# Revit family: Gira_045401
name_source: partatom
category: Electrical Fixtures
revit_build: Autodesk Revit 2017 (Build: 20160225_1515(x64)
units: mm (PartAtom-declared; Revit-internal decimal feet)

## family parameters
Cut with Voids When Loaded = No
Host = Face
Maintain Annotation Orientation = Yes
Part Type = Normal
Room Calculation Point = No
Round Connector Dimension = Use Diameter
Shared = No

## types (1)
- SCHUKO HC System 55 cr.white
    Available = No
    BIM (1) = https://media.stage.bim.site
    Category = Socket outlet
    Cremeweiß glänzend = Cremeweiß glänzend
    Data sheet (1) = https://katalog.gira.de
    Default Elevation = 1219 mm
    Description = SCHUKO HC Sys55 CW,SCHUKO socket outlet 16 A 250 V~ with hinged cover,,cream white glossy,Notes :,- In conjunction with the seal set and frame, 1-gang to 5-gang from the Standard 55 and Gira E2 design lines, flush-mounted SCHUKO socket outlets with hinged covers can be installed water-protected in accordance with IP44.
    GTIN = 4010337454014
    HAN = 045401
    HeinzeBIM = https://bimportal.heinze.de
    Manufacturer = Gira
    Manufacturer URL = https://www.gira.de
    Model = Protective contact (SCHUKO)
    Name = SCHUKO HC System 55 cr.white
    Transparent = No
    URL = http://katalog.gira.de

## geometry (parser evidence)
native form markers: Blend x2, Sweep x4
no freeform markers — native parametric forms only
